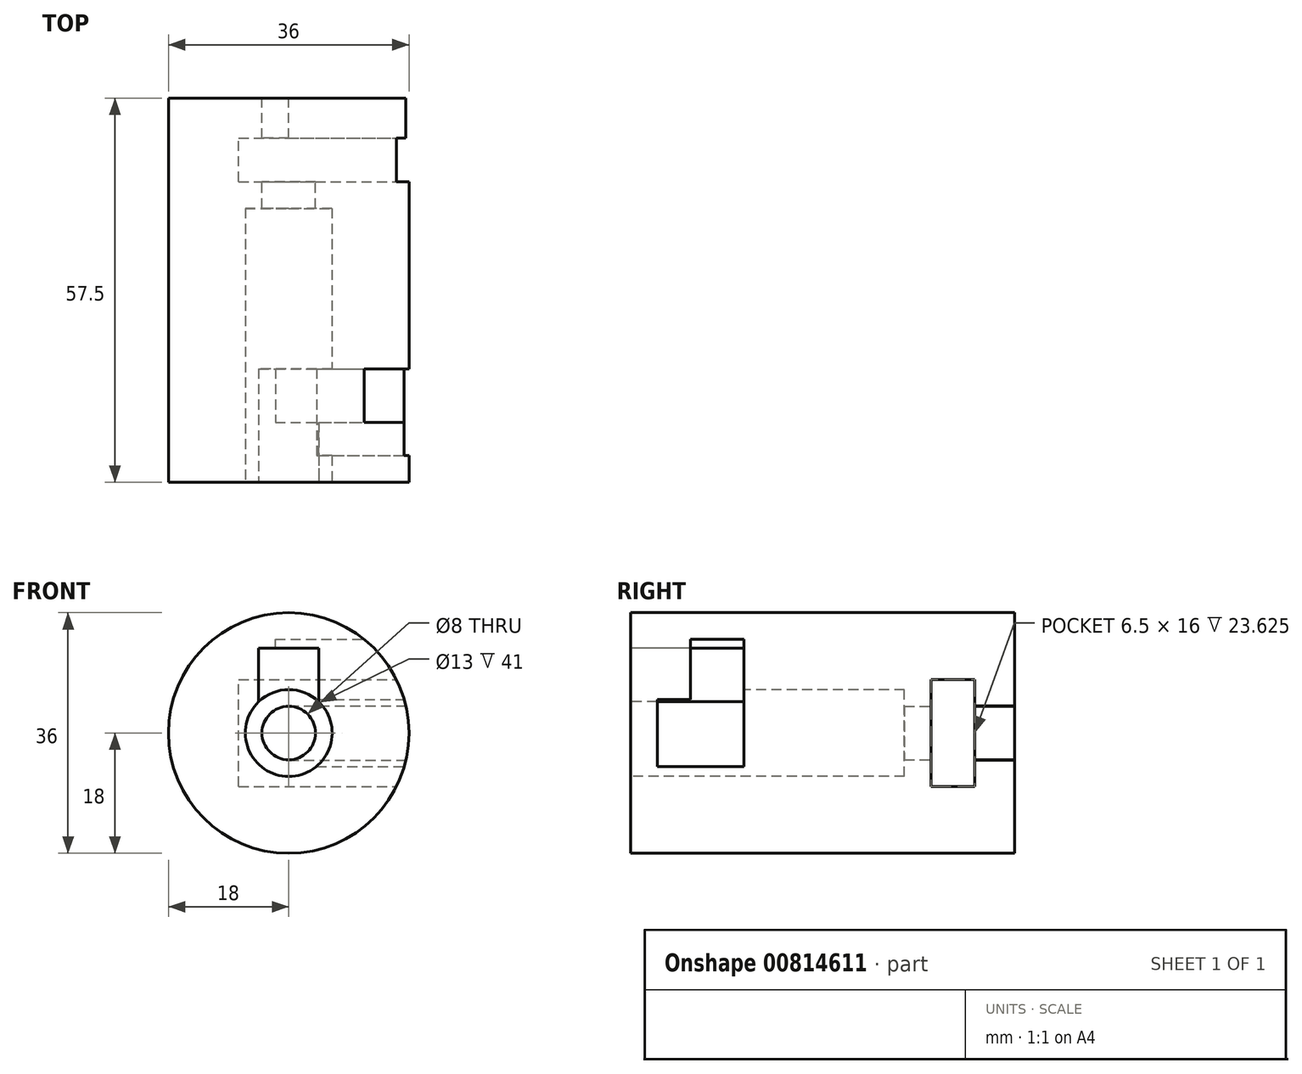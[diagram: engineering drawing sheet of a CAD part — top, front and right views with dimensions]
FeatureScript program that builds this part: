
annotation { "Feature Type Name" : "Feature", "Feature Type Description" : "" }
export const myFeature = defineFeature(function(context is Context, id is Id, definition is map)
    precondition{}
    {
        {
            var Q0;
            Q0=qCreatedBy(makeId("Front.planeOp"),FACE);
            var sketch = newSketch(context, id + "F0", { "sketchPlane" : qUnion([Q0])});
            skCircle(sketch, "E0", {"center": v(0, 0) * mm, "radius": 18 * mm});
            skCircle(sketch, "E1", {"center": v(0, 0) * mm, "radius": 6.5 * mm});
            skLineSegment(sketch, "E2.bottom", {"start": v(-4.5, 4.7) * mm, "end": v(4.5, 4.7) * mm});
            skLineSegment(sketch, "E2.top", {"start": v(-4.5, 12.7) * mm, "end": v(4.5, 12.7) * mm});
            skLineSegment(sketch, "E2.left", {"start": v(-4.5, 4.7) * mm, "end": v(-4.5, 12.7) * mm});
            skLineSegment(sketch, "E2.right", {"start": v(4.5, 4.7) * mm, "end": v(4.5, 12.7) * mm});
            skLineSegment(sketch, "E3", {"start": v(0, 4.7) * mm, "end": v(0, 12.7) * mm, "construction": true});
            skLineSegment(sketch, "E4", {"start": v(18, 0) * mm, "end": v(18, 34.55) * mm, "construction": true});
            skSolve(sketch);
        }
        {
            var Q0;
            Q0 = qSketchRegion(id + "F0", true);
            var Q1;
            Q1=makeQuery(id+"F0.imprint","IMPRINT",FACE,{"disambiguationData":[TD([[makeQuery(id+"F0.imprint","IMPRINT",EDGE,{"derivedFrom":sQuery(id+"F0.wireOp",EDGE,"E2.top")}),-1.0]])]});
            var Q2;
            {var subQ0=sQuery(id+"F0.wireOp",EDGE,"E2.bottom");Q2=makeQuery(id+"F0.imprint","IMPRINT",FACE,{"disambiguationData":[TD([[makeQuery(id+"F0.imprint","IMPRINT",EDGE,{"derivedFrom":subQ0}),-1.0]])]});}
            var Q3;
            {var subQ0=sQuery(id+"F0.wireOp",EDGE,"E2.bottom");Q3=makeQuery(id+"F0.imprint","IMPRINT",FACE,{"disambiguationData":[TD([[makeQuery(id+"F0.imprint","IMPRINT",EDGE,{"derivedFrom":subQ0}),1.0]])]});}
            extrude(context, id + "F1", {"entities" : qUnion([Q0, Q1, Q2, Q3]), "oppositeDirection" : true, "depth" : 57.5 * mm, "offsetDistance" : 25 * mm});
        }
        {
            var Q0;
            {var subQ0=sQuery(id+"F0.wireOp",EDGE,"E2.bottom");Q0=makeQuery(id+"F0.imprint","IMPRINT",FACE,{"disambiguationData":[TD([[makeQuery(id+"F0.imprint","IMPRINT",EDGE,{"derivedFrom":subQ0}),-1.0]])]});}
            var Q1;
            {var subQ0=sQuery(id+"F0.wireOp",EDGE,"E2.bottom");Q1=makeQuery(id+"F0.imprint","IMPRINT",FACE,{"disambiguationData":[TD([[makeQuery(id+"F0.imprint","IMPRINT",EDGE,{"derivedFrom":subQ0}),1.0]])]});}
            extrude(context, id + "F2", {"entities" : qUnion([Q0, Q1]), "operationType" : NewBodyOperationType.REMOVE, "oppositeDirection" : true, "depth" : 41 * mm, "offsetDistance" : 25 * mm});
        }
        {
            var Q0;
            Q0=makeQuery(id+"F0.imprint","IMPRINT",FACE,{"disambiguationData":[TD([[makeQuery(id+"F0.imprint","IMPRINT",EDGE,{"derivedFrom":sQuery(id+"F0.wireOp",EDGE,"E2.top")}),-1.0]])]});
            extrude(context, id + "F3", {"entities" : qUnion([Q0]), "operationType" : NewBodyOperationType.REMOVE, "oppositeDirection" : true, "depth" : 17 * mm, "offsetDistance" : 25 * mm});
        }
        {
            var Q0;
            Q0=sQuery(id+"F0.wireOp",EDGE,"E4");
            cPlane(context, id + "F4", {"entities" : qUnion([Q0]), "cplaneType" : CPlaneType.LINE_ANGLE, "offset" : 25 * mm, "angle" : 0 * degree, "width" : 150 * mm, "height" : 150 * mm});
        }
        {
            var Q0;
            Q0=qCreatedBy(id+"F4.planeOp",FACE);
            var sketch = newSketch(context, id + "F5", { "sketchPlane" : qUnion([Q0])});
            skLineSegment(sketch, "E5.bottom", {"start": v(4, -5) * mm, "end": v(17, -5) * mm});
            skLineSegment(sketch, "E5.top", {"start": v(4, 5) * mm, "end": v(17, 5) * mm});
            skLineSegment(sketch, "E5.left", {"start": v(4, -5) * mm, "end": v(4, 5) * mm});
            skLineSegment(sketch, "E5.right", {"start": v(17, -5) * mm, "end": v(17, 5) * mm});
            skLineSegment(sketch, "E6", {"start": v(17, 0) * mm, "end": v(4, 0) * mm, "construction": true});
            skLineSegment(sketch, "E7.bottom", {"start": v(9, 5) * mm, "end": v(17, 5) * mm});
            skLineSegment(sketch, "E7.top", {"start": v(9, 14) * mm, "end": v(17, 14) * mm});
            skLineSegment(sketch, "E7.left", {"start": v(9, 5) * mm, "end": v(9, 14) * mm});
            skLineSegment(sketch, "E7.right", {"start": v(17, 5) * mm, "end": v(17, 14) * mm});
            skSolve(sketch);
        }
        {
            var Q0;
            Q0=makeQuery(id+"F5.imprint","IMPRINT",FACE,{"disambiguationData":[TD([[makeQuery(id+"F5.imprint","IMPRINT",EDGE,{"derivedFrom":sQuery(id+"F5.wireOp",EDGE,"E5.bottom")}),1.0]])]});
            var Q1;
            Q1=makeQuery(id+"F5.imprint","IMPRINT",FACE,{"disambiguationData":[TD([[makeQuery(id+"F5.imprint","IMPRINT",EDGE,{"derivedFrom":sQuery(id+"F5.wireOp",EDGE,"E7.top")}),-1.0]])]});
            extrude(context, id + "F6", {"entities" : qUnion([Q0, Q1]), "operationType" : NewBodyOperationType.REMOVE, "oppositeDirection" : true, "depth" : 20 * mm, "offsetDistance" : 25 * mm});
        }
        {
            var Q0;
            Q0=makeQuery(id+"F1.opExtrude","CAP_FACE",FACE,{"disambiguationData":[OSD([sQuery(id+"F0.wireOp",EDGE,"E0")])],"isStart":false});
            var sketch = newSketch(context, id + "F7", { "sketchPlane" : qUnion([Q0])});
            skCircle(sketch, "E8", {"center": v(0, 0) * mm, "radius": 4 * mm});
            skCircle(sketch, "E9.cCircle", {"center": v(0, 0) * mm, "radius": 6.5 * mm, "construction": true});
            skLineSegment(sketch, "E9.0", {"start": v(7.5, 0) * mm, "end": v(3.75, -6.5) * mm});
            skLineSegment(sketch, "E9.1", {"start": v(3.75, -6.5) * mm, "end": v(-3.75, -6.5) * mm});
            skLineSegment(sketch, "E9.2", {"start": v(-3.75, -6.5) * mm, "end": v(-7.5, 0) * mm});
            skLineSegment(sketch, "E9.3", {"start": v(-7.5, 0) * mm, "end": v(-3.75, 6.5) * mm});
            skLineSegment(sketch, "E9.4", {"start": v(-3.75, 6.5) * mm, "end": v(3.75, 6.5) * mm});
            skLineSegment(sketch, "E9.5", {"start": v(3.75, 6.5) * mm, "end": v(7.5, 0) * mm});
            skPoint(sketch, "E9.0.midPoint", {"position": v(5.62, -3.25) * mm});
            skSolve(sketch);
        }
        {
            var Q0;
            Q0=makeQuery(id+"F7.imprint","IMPRINT",FACE,{"disambiguationData":[TD([[makeQuery(id+"F7.imprint","IMPRINT",EDGE,{"derivedFrom":sQuery(id+"F7.wireOp",EDGE,"E8")}),1.0]])]});
            extrude(context, id + "F8", {"entities" : qUnion([Q0]), "operationType" : NewBodyOperationType.REMOVE, "oppositeDirection" : true, "depth" : 17 * mm, "offsetDistance" : 25 * mm});
        }
        {
            var Q0;
            Q0=qCreatedBy(id+"F4.planeOp",FACE);
            var sketch = newSketch(context, id + "F9", { "sketchPlane" : qUnion([Q0])});
            skLineSegment(sketch, "E10.bottom", {"start": v(45, -8) * mm, "end": v(51.5, -8) * mm});
            skLineSegment(sketch, "E10.top", {"start": v(45, 8) * mm, "end": v(51.5, 8) * mm});
            skLineSegment(sketch, "E10.left", {"start": v(45, -8) * mm, "end": v(45, 8) * mm});
            skLineSegment(sketch, "E10.right", {"start": v(51.5, -8) * mm, "end": v(51.5, 8) * mm});
            skLineSegment(sketch, "E11", {"start": v(45, 0) * mm, "end": v(51.5, 0) * mm, "construction": true});
            skLineSegment(sketch, "E12.bottom", {"start": v(57.5, 4.05) * mm, "end": v(45, 4.05) * mm});
            skLineSegment(sketch, "E12.top", {"start": v(57.5, -4.05) * mm, "end": v(45, -4.05) * mm});
            skLineSegment(sketch, "E12.left", {"start": v(57.5, 4.05) * mm, "end": v(57.5, -4.05) * mm});
            skLineSegment(sketch, "E12.right", {"start": v(45, 4.05) * mm, "end": v(45, -4.05) * mm});
            skPoint(sketch, "E12.middle", {"position": v(51.5, 0) * mm});
            skSolve(sketch);
        }
        {
            var Q0;
            {var subQ0=sQuery(id+"F9.wireOp",EDGE,"E10.bottom");Q0=makeQuery(id+"F9.imprint","IMPRINT",FACE,{"disambiguationData":[TD([[makeQuery(id+"F9.imprint","IMPRINT",EDGE,{"derivedFrom":subQ0}),1.0]])]});}
            var Q1;
            {var subQ0=sQuery(id+"F9.wireOp",EDGE,"E12.top");var subQ1=sQuery(id+"F9.wireOp",EDGE,"E10.left");var subQ2=makeQuery(id+"F9.imprint","INTERSECT",VERTEX,{"derivedFrom":[subQ1,subQ0]});Q1=makeQuery(id+"F9.imprint","IMPRINT",FACE,{"disambiguationData":[TD([[makeQuery(id+"F9.imprint","IMPRINT",EDGE,{"disambiguationData":[TD([[subQ2,-1.0]])],"derivedFrom":subQ1}),-1.0]])]});}
            var Q2;
            {var subQ0=sQuery(id+"F9.wireOp",EDGE,"E10.top");Q2=makeQuery(id+"F9.imprint","IMPRINT",FACE,{"disambiguationData":[TD([[makeQuery(id+"F9.imprint","IMPRINT",EDGE,{"derivedFrom":subQ0}),-1.0]])]});}
            var Q3;
            Q3=sQuery(id+"F7.wireOp",VERTEX,"E9.0.start");
            extrude(context, id + "F10", {"entities" : qUnion([Q0, Q1, Q2]), "operationType" : NewBodyOperationType.REMOVE, "endBound" : BoundingType.UP_TO_VERTEX, "oppositeDirection" : true, "depth" : 25 * mm, "endBoundEntityVertex" : qUnion([Q3]), "offsetDistance" : 25 * mm});
        }
        {
            var Q0;
            {var subQ0=sQuery(id+"F9.wireOp",EDGE,"E12.top");var subQ1=sQuery(id+"F9.wireOp",EDGE,"E10.left");var subQ2=makeQuery(id+"F9.imprint","INTERSECT",VERTEX,{"derivedFrom":[subQ1,subQ0]});Q0=makeQuery(id+"F9.imprint","IMPRINT",FACE,{"disambiguationData":[TD([[makeQuery(id+"F9.imprint","IMPRINT",EDGE,{"disambiguationData":[TD([[subQ2,-1.0]])],"derivedFrom":subQ1}),-1.0]])]});}
            var Q1;
            {var subQ5=sQuery(id+"F9.wireOp",EDGE,"E12.left");Q1=makeQuery(id+"F9.imprint","IMPRINT",FACE,{"disambiguationData":[TD([[makeQuery(id+"F9.imprint","IMPRINT",EDGE,{"derivedFrom":subQ5}),-1.0]])]});}
            var Q2;
            Q2=makeQuery(id+"F10.boolean.opBoolean","SPLIT",FACE,{"disambiguationData":[TD([makeQuery(id+"F1.opExtrude","CAP_FACE",FACE,{"disambiguationData":[OSD([sQuery(id+"F0.wireOp",EDGE,"E0")])],"isStart":false})])],"derivedFrom":makeQuery(id+"F8.boolean.opBoolean","COPY",FACE,{"derivedFrom":makeQuery(id+"F8.opExtrude","SWEPT_FACE",FACE,{"disambiguationData":[OSD([sQuery(id+"F7.wireOp",EDGE,"E8")])]})})});
            var Q3;
            Q3=sQuery(id+"F7.wireOp",VERTEX,"E8.center");
            extrude(context, id + "F11", {"entities" : qUnion([Q0, Q1]), "operationType" : NewBodyOperationType.REMOVE, "endBound" : BoundingType.UP_TO_VERTEX, "oppositeDirection" : true, "depth" : 20 * mm, "endBoundEntityFace" : qUnion([Q2]), "endBoundEntityVertex" : qUnion([Q3]), "offsetDistance" : 25 * mm});
        }
    });
